# Revit family: Sanitary_Screens-Dividers_Stern-Engineering_WC-Cubicles1
name_source: partatom
category: Specialty Equipment
units: mm (PartAtom-declared; Revit-internal decimal feet)

## family parameters
Always vertical = Yes
Cut with Voids When Loaded = No
OmniClass Number = 23.25.40.14.14
OmniClass Title = Sanitary Partitions and Cubicles
Part Type = Normal
Room Calculation Point = No
Round Connector Dimension = Use Diameter
Shared = No
Work Plane-Based = Yes

## types (1)
- Default – Create Custom Cubicles
    Apparent Load = 0 VA
    Current = 0 A
    Default Elevation = 0 mm  [stored 0 ft]
    Description = Fully integrated access system that offers door control from the exterior and interior of the cubicle using hand proximity sensors. The sensor and LED indicator mechanism on the exterior of the system resembles a standard door lock. On the interior of the door, the sensor and LED indicator mechanism appear as a regular circular handle. The system runs using 24 volt electrical power using a transformer from the main power source for up to 4 cubicles together. Wiring happens during manufacturing, no wiring is requiring during the installation.
    Manufacturer = Stern Engineering
    Model = Touchless WC Cubicles
    Number of Poles = 1
    Power Connector Description = Power Connection
    Power Factor = 1
    Product data url = https://bimobject.com
    URL = https://sternfaucets.com
    Version = 1
    Voltage = 15 V

note: [stored X ft] marks values corroborated as IEEE doubles in the binary element streams (Revit-internal decimal feet)

## geometry (parser evidence)
native form markers: Sweep x10
no freeform markers — native parametric forms only
